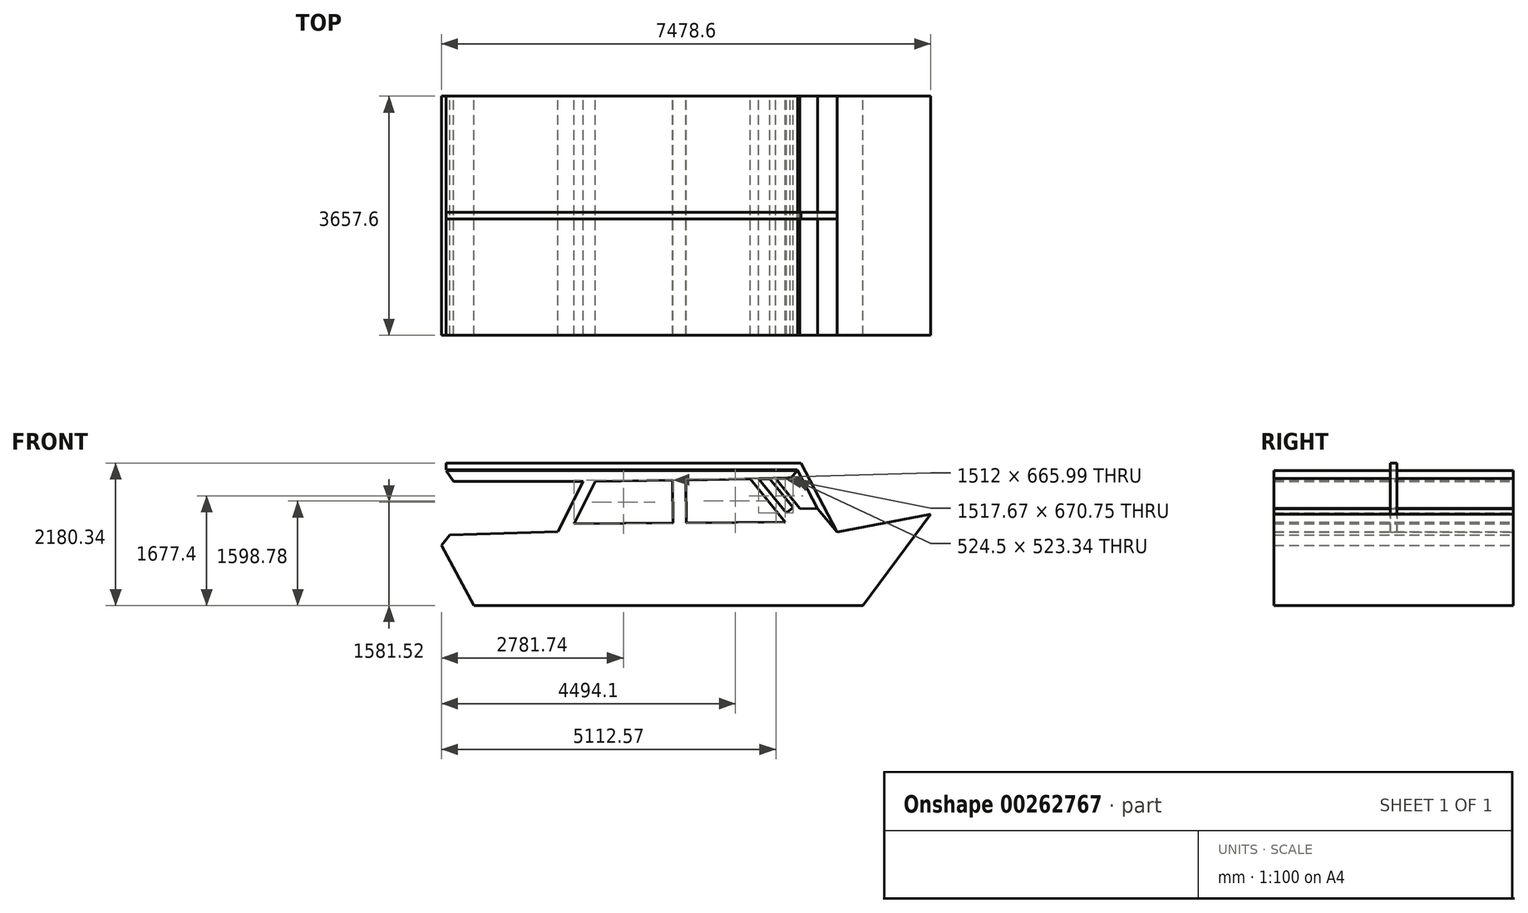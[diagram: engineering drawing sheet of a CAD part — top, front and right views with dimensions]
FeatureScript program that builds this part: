
annotation { "Feature Type Name" : "Feature", "Feature Type Description" : "" }
export const myFeature = defineFeature(function(context is Context, id is Id, definition is map)
    precondition{}
    {
        {
            var Q0;
            Q0=qCreatedBy(makeId("Front.planeOp"),FACE);
            var sketch = newSketch(context, id + "F0", { "sketchPlane" : qUnion([Q0])});
            skLineSegment(sketch, "E0", {"start": v(-3802.73, 13.95) * mm, "end": v(3817.27, 13.95) * mm, "construction": true});
            skLineSegment(sketch, "E1", {"start": v(-3672.94, 171.36) * mm, "end": v(-2020.35, 223.86) * mm});
            skLineSegment(sketch, "E2", {"start": v(-2020.35, 223.86) * mm, "end": v(-1637.73, 989) * mm});
            skLineSegment(sketch, "E3", {"start": v(-3730.9, 1155.05) * mm, "end": v(1642.69, 1155.94) * mm});
            skLineSegment(sketch, "E4", {"start": v(1642.69, 1155.94) * mm, "end": v(1527.56, 1038.2) * mm});
            skLineSegment(sketch, "E5", {"start": v(-1776.98, 342.54) * mm, "end": v(-264.99, 355.65) * mm});
            skLineSegment(sketch, "E6", {"start": v(1450.2, 370.52) * mm, "end": v(919.34, 1028.16) * mm});
            skLineSegment(sketch, "E7", {"start": v(-1776.98, 342.54) * mm, "end": v(-1453.71, 989) * mm});
            skLineSegment(sketch, "E8", {"start": v(1304.83, 1034.52) * mm, "end": v(1671.47, 580.33) * mm});
            skLineSegment(sketch, "E9", {"start": v(1671.47, 580.33) * mm, "end": v(1944.65, 572.37) * mm});
            skLineSegment(sketch, "E10", {"start": v(1944.65, 572.37) * mm, "end": v(2242.79, 218.26) * mm});
            skLineSegment(sketch, "E11", {"start": v(2242.79, 218.26) * mm, "end": v(3675.87, 490.31) * mm});
            skLineSegment(sketch, "E12", {"start": v(3675.87, 490.31) * mm, "end": v(2638.15, -905.99) * mm});
            skLineSegment(sketch, "E13", {"start": v(2638.15, -905.99) * mm, "end": v(-3305.62, -905.99) * mm});
            skLineSegment(sketch, "E14", {"start": v(-3305.62, -905.99) * mm, "end": v(-3802.73, 13.95) * mm});
            skLineSegment(sketch, "E15", {"start": v(-3672.94, 171.36) * mm, "end": v(-3802.73, 13.95) * mm});
            skLineSegment(sketch, "E16", {"start": v(1047.6, 1030.4) * mm, "end": v(1467.89, 509.74) * mm});
            skLineSegment(sketch, "E17", {"start": v(1467.89, 509.74) * mm, "end": v(1572.1, 593.86) * mm});
            skLineSegment(sketch, "E18", {"start": v(1572.1, 593.86) * mm, "end": v(1217.53, 1033.08) * mm});
            skLineSegment(sketch, "E19", {"start": v(-3730.9, 1155.05) * mm, "end": v(-3614.66, 989) * mm});
            skLineSegment(sketch, "E20", {"start": v(-1637.73, 989) * mm, "end": v(-3614.66, 989) * mm});
            skLineSegment(sketch, "E21", {"start": v(1527.56, 1038.2) * mm, "end": v(1304.83, 1034.52) * mm});
            skPoint(sketch, "E22.orphan", {"position": v(1301.86, 1038.2) * mm});
            skLineSegment(sketch, "E23", {"start": v(-163.39, 356.53) * mm, "end": v(-169.06, 1010.2) * mm, "construction": true});
            skLineSegment(sketch, "E24.0", {"start": v(-61.8, 357.41) * mm, "end": v(-67.47, 1011.88) * mm});
            skLineSegment(sketch, "E25.0", {"start": v(-264.99, 355.65) * mm, "end": v(-270.66, 1009.32) * mm});
            skLineSegment(sketch, "E26.trimOffspring", {"start": v(-270.65, 1008.53) * mm, "end": v(-1453.71, 989) * mm});
            skLineSegment(sketch, "E27.trimOffspring", {"start": v(-61.8, 357.41) * mm, "end": v(1450.2, 370.52) * mm});
            skLineSegment(sketch, "E28.trimOffspring", {"start": v(919.34, 1028.16) * mm, "end": v(-67.47, 1011.88) * mm});
            skLineSegment(sketch, "E29", {"start": v(1047.6, 1030.4) * mm, "end": v(1217.53, 1033.08) * mm});
            skSolve(sketch);
        }
        {
            var Q0;
            Q0=makeQuery(id+"F0.imprint","IMPRINT",FACE,{"disambiguationData":[TD([[makeQuery(id+"F0.imprint","IMPRINT",EDGE,{"derivedFrom":sQuery(id+"F0.wireOp",EDGE,"E1")}),-1.0]])]});
            extrude(context, id + "F1", {"entities" : qUnion([Q0]), "endBound" : BoundingType.SYMMETRIC, "depth" : 3657.6 * mm});
        }
        {
            var Q0;
            Q0=qCreatedBy(makeId("Front.planeOp"),FACE);
            var sketch = newSketch(context, id + "F2", { "sketchPlane" : qUnion([Q0])});
            skLineSegment(sketch, "E30.0", {"start": v(1944.65, 572.37) * mm, "end": v(2242.79, 218.26) * mm});
            skLineSegment(sketch, "E31", {"start": v(2242.79, 218.26) * mm, "end": v(1694.96, 1274.35) * mm});
            skLineSegment(sketch, "E32", {"start": v(1633.21, 1172.75) * mm, "end": v(-3729.11, 1172.75) * mm});
            skLineSegment(sketch, "E33", {"start": v(1944.65, 572.37) * mm, "end": v(1633.21, 1172.75) * mm});
            skLineSegment(sketch, "E34.0", {"start": v(1694.96, 1274.35) * mm, "end": v(-3729.11, 1274.35) * mm});
            skLineSegment(sketch, "E35", {"start": v(-2554.08, 6442.33) * mm, "end": v(-2492.95, 6523.48) * mm});
            skLineSegment(sketch, "E36", {"start": v(-3729.11, 1274.35) * mm, "end": v(-3729.11, 1172.75) * mm});
            skSolve(sketch);
        }
        {
            var Q0;
            Q0 = qSketchRegion(id + "F2", true);
            extrude(context, id + "F3", {"entities" : qUnion([Q0]), "operationType" : NewBodyOperationType.ADD, "depth" : 50.8 * mm, "hasSecondDirection" : true, "secondDirectionOppositeDirection" : true, "secondDirectionDepth" : 50.8 * mm});
        }
    });
